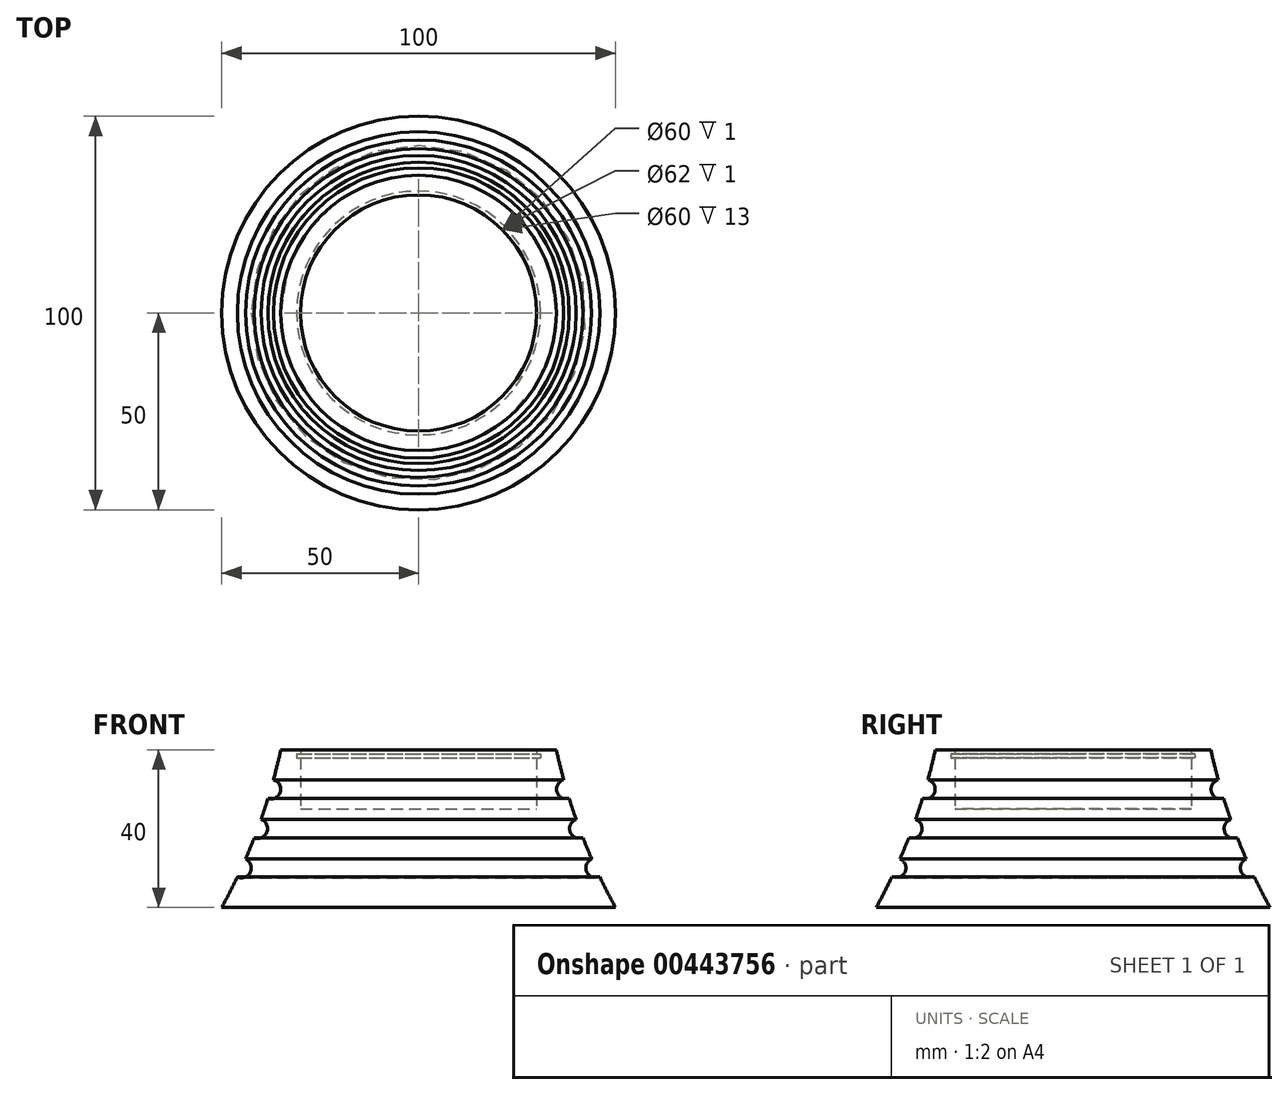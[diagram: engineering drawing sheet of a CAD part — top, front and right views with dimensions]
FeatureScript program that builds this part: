
annotation { "Feature Type Name" : "Feature", "Feature Type Description" : "" }
export const myFeature = defineFeature(function(context is Context, id is Id, definition is map)
    precondition{}
    {
        {
            var Q0;
            Q0=qCreatedBy(makeId("Front.planeOp"),FACE);
            var sketch = newSketch(context, id + "F0", { "sketchPlane" : qUnion([Q0])});
            skLineSegment(sketch, "E0", {"start": v(0, 0) * mm, "end": v(50, 0) * mm});
            skLineSegment(sketch, "E1", {"start": v(0, 0) * mm, "end": v(0, 25) * mm});
            skLineSegment(sketch, "E2", {"start": v(0, 25) * mm, "end": v(30, 25) * mm});
            skLineSegment(sketch, "E3", {"start": v(30, 25) * mm, "end": v(30, 38) * mm});
            skLineSegment(sketch, "E4", {"start": v(30, 38) * mm, "end": v(31, 38) * mm});
            skLineSegment(sketch, "E5", {"start": v(31, 38) * mm, "end": v(31, 39) * mm});
            skLineSegment(sketch, "E6", {"start": v(31, 39) * mm, "end": v(30, 39) * mm});
            skLineSegment(sketch, "E7", {"start": v(30, 39) * mm, "end": v(30, 40) * mm});
            skLineSegment(sketch, "E8", {"start": v(30, 40) * mm, "end": v(35, 40) * mm});
            skArc(sketch, "E9", {"start": v(35, 40) * mm, "mid": v(35.89, 36.2) * mm, "end": v(36.87, 32.4) * mm});
            skArc(sketch, "E10", {"start": v(36.87, 32.4) * mm, "mid": v(35.16, 29.3) * mm, "end": v(38.28, 27.6) * mm});
            skArc(sketch, "E11", {"start": v(40.02, 22.35) * mm, "mid": v(38.52, 19.13) * mm, "end": v(41.76, 17.66) * mm});
            skArc(sketch, "E12", {"start": v(43.97, 12.28) * mm, "mid": v(42.72, 8.96) * mm, "end": v(46.05, 7.73) * mm});
            skArc(sketch, "E13.trimOffspring", {"start": v(46.05, 7.73) * mm, "mid": v(47.97, 3.84) * mm, "end": v(50, 0) * mm});
            skArc(sketch, "E14.trimOffspring", {"start": v(41.76, 17.66) * mm, "mid": v(42.84, 14.96) * mm, "end": v(43.97, 12.28) * mm});
            skArc(sketch, "E15.trimOffspring", {"start": v(38.28, 27.6) * mm, "mid": v(39.12, 24.97) * mm, "end": v(40.02, 22.35) * mm});
            skSolve(sketch);
        }
        {
            var Q0;
            Q0 = qSketchRegion(id + "F0", true);
            var Q1;
            Q1=sQuery(id+"F0.wireOp",EDGE,"E1");
            revolve(context, id + "F1", {"entities" : qUnion([Q0]), "axis" : qUnion([Q1]), "revolveType" : RevolveType.FULL});
        }
    });
